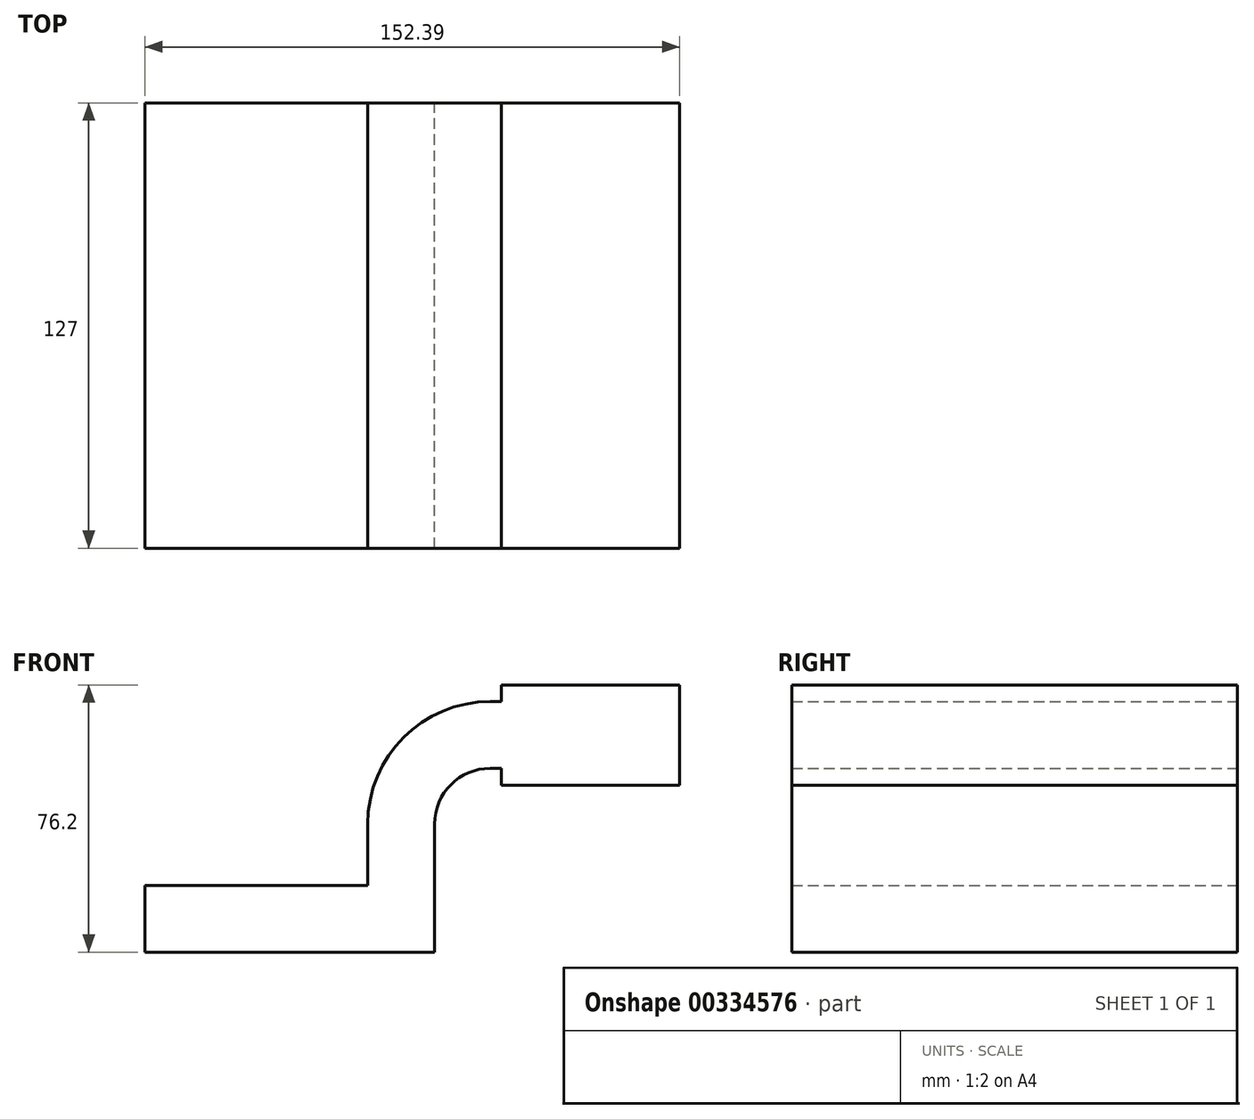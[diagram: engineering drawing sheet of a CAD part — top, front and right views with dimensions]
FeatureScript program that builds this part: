
annotation { "Feature Type Name" : "Feature", "Feature Type Description" : "" }
export const myFeature = defineFeature(function(context is Context, id is Id, definition is map)
    precondition{}
    {
        {
            var Q0;
            Q0=qCreatedBy(makeId("Front.planeOp"),FACE);
            var sketch = newSketch(context, id + "F0", { "sketchPlane" : qUnion([Q0])});
            skLineSegment(sketch, "E0.bottom", {"start": v(-41.27, -9.53) * mm, "end": v(41.28, -9.53) * mm});
            skLineSegment(sketch, "E0.top", {"start": v(-41.28, 9.52) * mm, "end": v(41.28, 9.52) * mm});
            skLineSegment(sketch, "E0.left", {"start": v(-41.28, -9.53) * mm, "end": v(-41.28, 9.53) * mm});
            skLineSegment(sketch, "E0.right", {"start": v(41.28, -9.53) * mm, "end": v(41.28, 9.52) * mm});
            skPoint(sketch, "E0.middle", {"position": v(0, 0) * mm});
            skLineSegment(sketch, "E1.bottom", {"start": v(111.12, 38.1) * mm, "end": v(60.32, 38.1) * mm});
            skLineSegment(sketch, "E1.top", {"start": v(111.12, 66.67) * mm, "end": v(60.32, 66.67) * mm});
            skLineSegment(sketch, "E1.left", {"start": v(111.12, 38.1) * mm, "end": v(111.12, 66.67) * mm});
            skLineSegment(sketch, "E1.right", {"start": v(60.32, 38.1) * mm, "end": v(60.32, 66.67) * mm});
            skPoint(sketch, "E1.middle", {"position": v(85.72, 52.39) * mm});
            skLineSegment(sketch, "E2", {"start": v(41.28, 9.52) * mm, "end": v(41.28, 27) * mm});
            skArc(sketch, "E3", {"start": v(41.27, 27) * mm, "mid": v(45.92, 38.23) * mm, "end": v(57.15, 42.88) * mm});
            skLineSegment(sketch, "E4", {"start": v(57.15, 42.88) * mm, "end": v(80.48, 42.88) * mm});
            skLineSegment(sketch, "E5.0", {"start": v(57.15, 61.93) * mm, "end": v(80.48, 61.93) * mm});
            skArc(sketch, "E5.1", {"start": v(22.22, 27) * mm, "mid": v(32.45, 51.7) * mm, "end": v(57.15, 61.93) * mm});
            skLineSegment(sketch, "E5.2", {"start": v(22.23, 9.52) * mm, "end": v(22.23, 27) * mm});
            skLineSegment(sketch, "E6", {"start": v(80.48, 42.88) * mm, "end": v(80.48, 61.93) * mm});
            skFitSpline(sketch, "E7", {"points": [v(-41.28, 9.53) * mm, v(57.15, 61.93) * mm], "startDerivative": vector(50.47, 142.16) * mm, "endDerivative": vector(129.72, -19.1) * mm});
            skSolve(sketch);
        }
        {
            var Q0;
            {var subQ0=sQuery(id+"F0.wireOp",EDGE,"E2");Q0=makeQuery(id+"F0.imprint","IMPRINT",FACE,{"disambiguationData":[TD([[makeQuery(id+"F0.imprint","IMPRINT",EDGE,{"derivedFrom":subQ0}),1.0]])]});}
            var Q1;
            Q1=makeQuery(id+"F0.imprint","IMPRINT",FACE,{"disambiguationData":[TD([[makeQuery(id+"F0.imprint","IMPRINT",EDGE,{"derivedFrom":sQuery(id+"F0.wireOp",EDGE,"E5.1")}),1.0]])]});
            var Q2;
            {var subQ5=sQuery(id+"F0.wireOp",EDGE,"E6");Q2=makeQuery(id+"F0.imprint","IMPRINT",FACE,{"disambiguationData":[TD([[makeQuery(id+"F0.imprint","IMPRINT",EDGE,{"derivedFrom":subQ5}),1.0]])]});}
            var Q3;
            {var subQ1=sQuery(id+"F0.wireOp",EDGE,"E1.bottom");Q3=makeQuery(id+"F0.imprint","IMPRINT",FACE,{"disambiguationData":[TD([[makeQuery(id+"F0.imprint","IMPRINT",EDGE,{"derivedFrom":subQ1}),-1.0]])]});}
            var Q4;
            Q4=makeQuery(id+"F0.imprint","IMPRINT",FACE,{"disambiguationData":[TD([[makeQuery(id+"F0.imprint","IMPRINT",EDGE,{"derivedFrom":sQuery(id+"F0.wireOp",EDGE,"E0.bottom")}),1.0]])]});
            extrude(context, id + "F1", {"entities" : qUnion([Q0, Q1, Q2, Q3, Q4]), "endBound" : BoundingType.SYMMETRIC, "depth" : 127 * mm});
        }
    });
